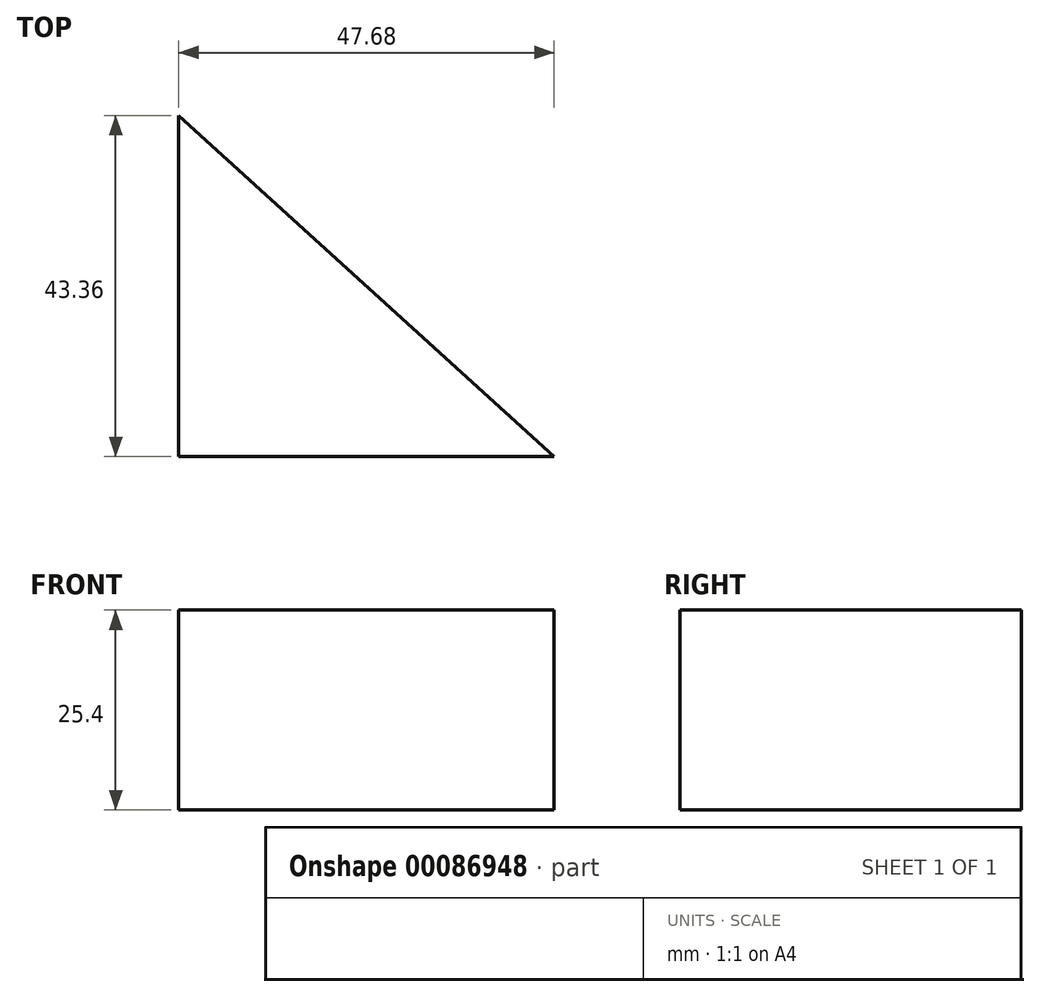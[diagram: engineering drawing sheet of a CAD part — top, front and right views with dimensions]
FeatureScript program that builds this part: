
annotation { "Feature Type Name" : "Feature", "Feature Type Description" : "" }
export const myFeature = defineFeature(function(context is Context, id is Id, definition is map)
    precondition{}
    {
        {
            var Q0;
            Q0=qCreatedBy(makeId("Top.planeOp"),FACE);
            var sketch = newSketch(context, id + "F0", { "sketchPlane" : qUnion([Q0])});
            skLineSegment(sketch, "E0", {"start": v(0, 0) * mm, "end": v(47.68, 0) * mm});
            skLineSegment(sketch, "E1", {"start": v(47.68, 0) * mm, "end": v(0, 43.36) * mm});
            skLineSegment(sketch, "E2", {"start": v(0, 43.36) * mm, "end": v(0, 0) * mm});
            skSolve(sketch);
        }
        {
            var Q0;
            Q0=makeQuery(id+"F0.imprint","IMPRINT",FACE,{"disambiguationData":[TD([[makeQuery(id+"F0.imprint","IMPRINT",EDGE,{"derivedFrom":sQuery(id+"F0.wireOp",EDGE,"E0")}),1.0]])]});
            extrude(context, id + "F1", {"entities" : qUnion([Q0]), "depth" : 25.4 * mm});
        }
    });
